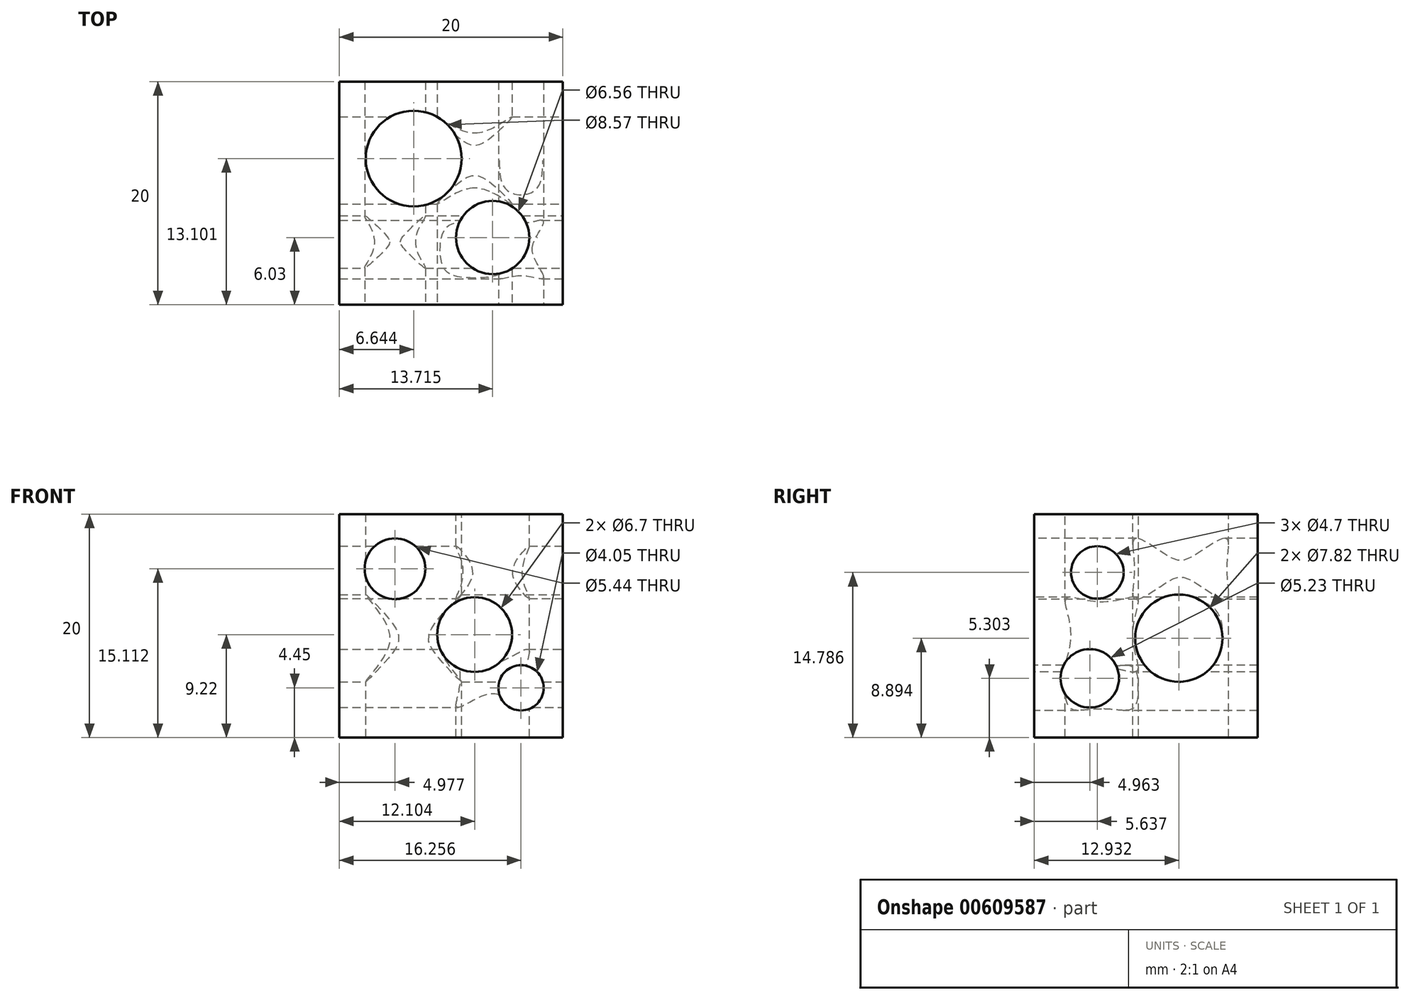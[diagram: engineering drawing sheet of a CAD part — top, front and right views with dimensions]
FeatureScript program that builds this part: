
annotation { "Feature Type Name" : "Feature", "Feature Type Description" : "" }
export const myFeature = defineFeature(function(context is Context, id is Id, definition is map)
    precondition{}
    {
        {
            var Q0;
            Q0=qCreatedBy(makeId("Front.planeOp"),FACE);
            var sketch = newSketch(context, id + "F0", { "sketchPlane" : qUnion([Q0])});
            skLineSegment(sketch, "E0.bottom", {"start": v(3.3, -1.1) * mm, "end": v(23.3, -1.1) * mm});
            skLineSegment(sketch, "E0.top", {"start": v(3.3, -21.1) * mm, "end": v(23.3, -21.1) * mm});
            skLineSegment(sketch, "E0.left", {"start": v(3.3, -1.1) * mm, "end": v(3.3, -21.1) * mm});
            skLineSegment(sketch, "E0.right", {"start": v(23.3, -1.1) * mm, "end": v(23.3, -21.1) * mm});
            skSolve(sketch);
        }
        {
            var Q0;
            Q0=makeQuery(id+"F0.imprint","IMPRINT",FACE,{"disambiguationData":[TD([[makeQuery(id+"F0.imprint","IMPRINT",EDGE,{"derivedFrom":sQuery(id+"F0.wireOp",EDGE,"E0.bottom")}),-1.0]])]});
            extrude(context, id + "F1", {"entities" : qUnion([Q0]), "depth" : 20 * mm, "offsetDistance" : 25 * mm});
        }
        {
            var Q0;
            Q0=makeQuery(id+"F1.opExtrude","CAP_FACE",FACE,{"disambiguationData":[OSD([sQuery(id+"F0.wireOp",EDGE,"E0.bottom"),sQuery(id+"F0.wireOp",EDGE,"E0.top"),sQuery(id+"F0.wireOp",EDGE,"E0.left"),sQuery(id+"F0.wireOp",EDGE,"E0.right")])],"isStart":false});
            var sketch = newSketch(context, id + "F2", { "sketchPlane" : qUnion([Q0])});
            skCircle(sketch, "E1", {"center": v(8.28, -5.99) * mm, "radius": 2.72 * mm});
            skCircle(sketch, "E2", {"center": v(15.4, -11.88) * mm, "radius": 3.35 * mm});
            skCircle(sketch, "E3", {"center": v(19.56, -16.65) * mm, "radius": 2.03 * mm});
            skSolve(sketch);
        }
        {
            var Q0;
            Q0=makeQuery(id+"F2.imprint","IMPRINT",FACE,{"disambiguationData":[TD([[makeQuery(id+"F2.imprint","IMPRINT",EDGE,{"derivedFrom":sQuery(id+"F2.wireOp",EDGE,"E1")}),1.0]])]});
            var Q1;
            Q1=makeQuery(id+"F2.imprint","IMPRINT",FACE,{"disambiguationData":[TD([[makeQuery(id+"F2.imprint","IMPRINT",EDGE,{"derivedFrom":sQuery(id+"F2.wireOp",EDGE,"E2")}),1.0]])]});
            var Q2;
            Q2=makeQuery(id+"F2.imprint","IMPRINT",FACE,{"disambiguationData":[TD([[makeQuery(id+"F2.imprint","IMPRINT",EDGE,{"derivedFrom":sQuery(id+"F2.wireOp",EDGE,"E3")}),1.0]])]});
            extrude(context, id + "F3", {"entities" : qUnion([Q0, Q1, Q2]), "operationType" : NewBodyOperationType.REMOVE, "endBound" : BoundingType.THROUGH_ALL, "oppositeDirection" : true, "depth" : 25 * mm, "offsetDistance" : 25 * mm});
        }
        {
            var Q0;
            Q0=makeQuery(id+"F1.opExtrude","SWEPT_FACE",FACE,{"disambiguationData":[OSD([sQuery(id+"F0.wireOp",EDGE,"E0.right")])]});
            var sketch = newSketch(context, id + "F4", { "sketchPlane" : qUnion([Q0])});
            skCircle(sketch, "E4", {"center": v(-14.36, -6.31) * mm, "radius": 2.35 * mm});
            skCircle(sketch, "E5", {"center": v(-7.07, -12.2) * mm, "radius": 3.9 * mm});
            skCircle(sketch, "E6", {"center": v(-15.04, -15.8) * mm, "radius": 2.62 * mm});
            skSolve(sketch);
        }
        {
            var Q0;
            Q0=makeQuery(id+"F4.imprint","IMPRINT",FACE,{"disambiguationData":[TD([[makeQuery(id+"F4.imprint","IMPRINT",EDGE,{"derivedFrom":sQuery(id+"F4.wireOp",EDGE,"E4")}),1.0]])]});
            var Q1;
            Q1=makeQuery(id+"F4.imprint","IMPRINT",FACE,{"disambiguationData":[TD([[makeQuery(id+"F4.imprint","IMPRINT",EDGE,{"derivedFrom":sQuery(id+"F4.wireOp",EDGE,"E5")}),1.0]])]});
            var Q2;
            Q2=makeQuery(id+"F4.imprint","IMPRINT",FACE,{"disambiguationData":[TD([[makeQuery(id+"F4.imprint","IMPRINT",EDGE,{"derivedFrom":sQuery(id+"F4.wireOp",EDGE,"E6")}),1.0]])]});
            extrude(context, id + "F5", {"entities" : qUnion([Q0, Q1, Q2]), "operationType" : NewBodyOperationType.REMOVE, "endBound" : BoundingType.THROUGH_ALL, "oppositeDirection" : true, "depth" : 25 * mm, "offsetDistance" : 25 * mm});
        }
        {
            var Q0;
            Q0=makeQuery(id+"F1.opExtrude","SWEPT_FACE",FACE,{"disambiguationData":[OSD([sQuery(id+"F0.wireOp",EDGE,"E0.bottom")])]});
            var sketch = newSketch(context, id + "F6", { "sketchPlane" : qUnion([Q0])});
            skCircle(sketch, "E7", {"center": v(9.94, -6.9) * mm, "radius": 4.29 * mm});
            skCircle(sketch, "E8", {"center": v(17.02, -13.97) * mm, "radius": 3.28 * mm});
            skSolve(sketch);
        }
        {
            var Q0;
            Q0=makeQuery(id+"F6.imprint","IMPRINT",FACE,{"disambiguationData":[TD([[makeQuery(id+"F6.imprint","IMPRINT",EDGE,{"derivedFrom":sQuery(id+"F6.wireOp",EDGE,"E7")}),1.0]])]});
            var Q1;
            Q1=makeQuery(id+"F6.imprint","IMPRINT",FACE,{"disambiguationData":[TD([[makeQuery(id+"F6.imprint","IMPRINT",EDGE,{"derivedFrom":sQuery(id+"F6.wireOp",EDGE,"E8")}),1.0]])]});
            extrude(context, id + "F7", {"entities" : qUnion([Q0, Q1]), "operationType" : NewBodyOperationType.REMOVE, "endBound" : BoundingType.THROUGH_ALL, "oppositeDirection" : true, "depth" : 25 * mm, "offsetDistance" : 25 * mm});
        }
    });
